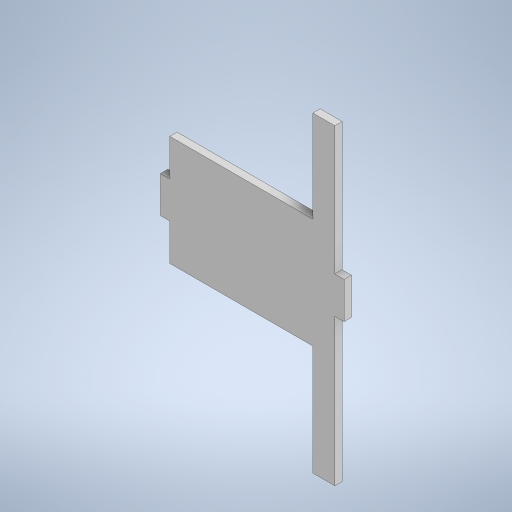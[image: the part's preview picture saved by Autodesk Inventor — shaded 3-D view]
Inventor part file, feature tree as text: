
AUTODESK INVENTOR PART (.ipt)
format: ipt  version: 2023.1 (Build 271208000, 208)  size: 258,560 bytes
history: native  units: mm
features: extrude x3, sketch x3
ambient origin geometry x8: Origin, YZ Plane, XZ Plane, XY Plane, X Axis, Y Axis, Z Axis, Center Point
bodies: 实体1 (feature_tree)
feature tree (6):
  extrude  "拉伸1"  Depth=850.0mm
  extrude  "拉伸2"  Depth=250.0mm
  extrude  "拉伸3"  Depth=20.0mm TaperAngle=0.0deg
  sketch  "草图1"  dims[d0=60.0mm d1=850.0mm]
  sketch  "草图2"  dims[d2=390.0mm d3=250.0mm]
  sketch  "草图3"  dims[d4=300.0mm d5=20.0mm d6=0.0mm d7=350.0mm d8=100.0mm d9=25.0mm d10=0.0mm d11=350.0mm d12=100.0mm d13=25.0mm d14=0.0mm]
